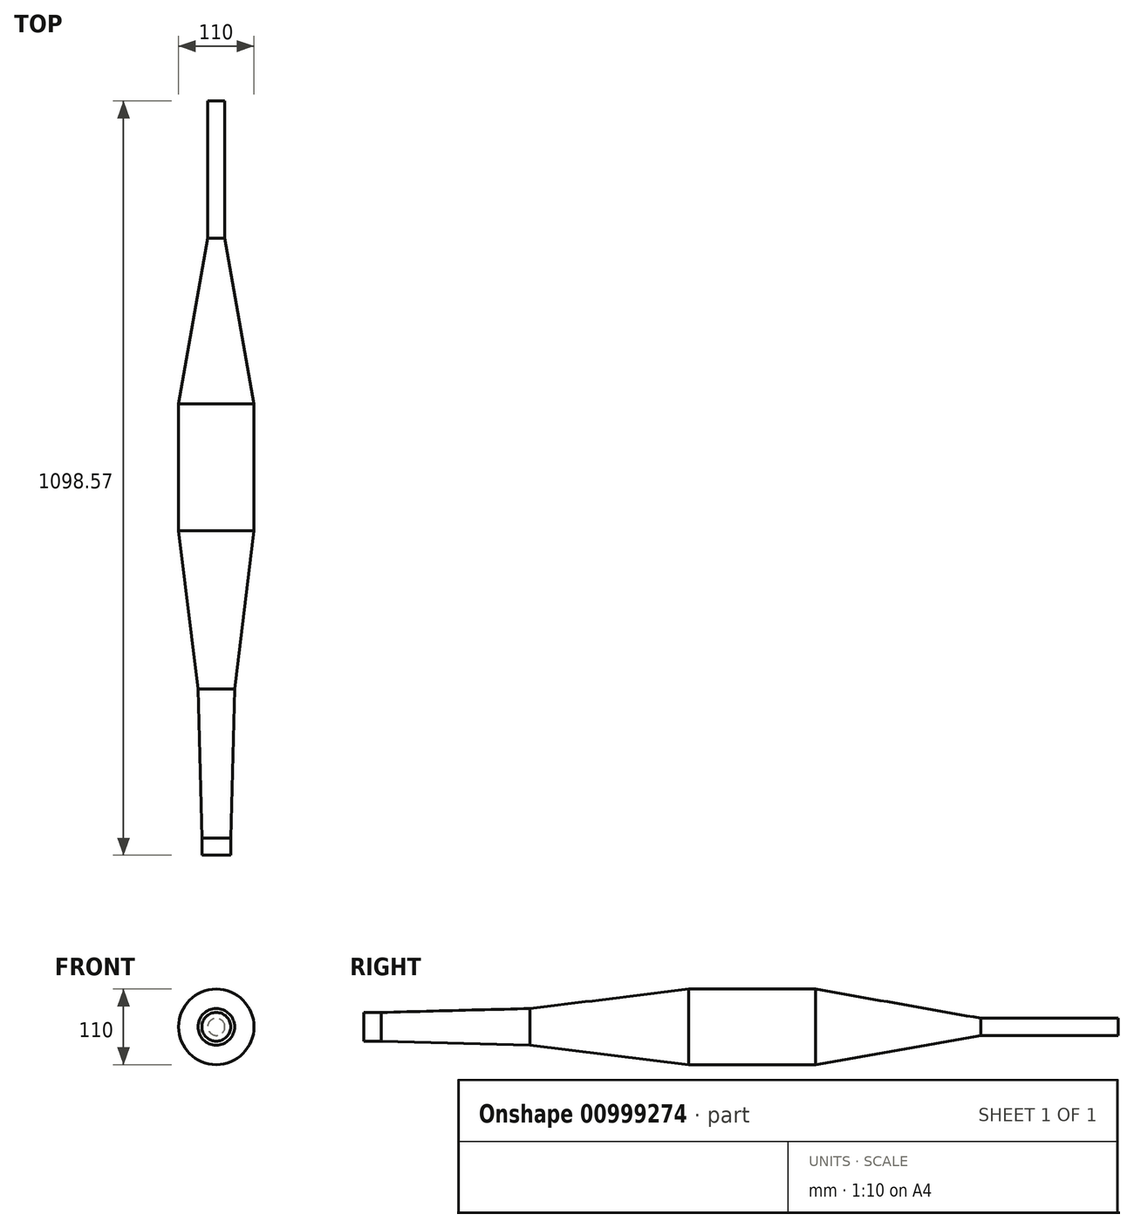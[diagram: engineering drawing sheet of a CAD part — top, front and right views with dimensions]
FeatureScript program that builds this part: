
annotation { "Feature Type Name" : "Feature", "Feature Type Description" : "" }
export const myFeature = defineFeature(function(context is Context, id is Id, definition is map)
    precondition{}
    {
        {
            var Q0;
            Q0=qCreatedBy(makeId("Right.planeOp"),FACE);
            var sketch = newSketch(context, id + "F0", { "sketchPlane" : qUnion([Q0])});
            skLineSegment(sketch, "E0", {"start": v(21.65, -12.5) * mm, "end": v(42.65, 23.87) * mm});
            skLineSegment(sketch, "E1", {"start": v(0, 191.98) * mm, "end": v(0, 233.98) * mm});
            skLineSegment(sketch, "E2", {"start": v(0, 212.98) * mm, "end": v(242, 212.98) * mm});
            skLineSegment(sketch, "E3", {"start": v(0, 212.98) * mm, "end": v(-65, 212.98) * mm});
            skLineSegment(sketch, "E4", {"start": v(242, 239.66) * mm, "end": v(242, 186.3) * mm});
            skLineSegment(sketch, "E5", {"start": v(25, 233.98) * mm, "end": v(242, 239.66) * mm});
            skLineSegment(sketch, "E6", {"start": v(25, 191.98) * mm, "end": v(242, 186.3) * mm});
            skLineSegment(sketch, "E7", {"start": v(-51.1, 50.44) * mm, "end": v(-51.1, 27.44) * mm});
            skLineSegment(sketch, "E8", {"start": v(-51.1, 38.94) * mm, "end": v(10.5, 18.19) * mm});
            skLineSegment(sketch, "E9", {"start": v(242, 212.98) * mm, "end": v(344.06, 212.98) * mm});
            skLineSegment(sketch, "E10", {"start": v(242, 239.66) * mm, "end": v(344.06, 252.2) * mm});
            skLineSegment(sketch, "E11", {"start": v(242, 186.3) * mm, "end": v(344.06, 173.76) * mm});
            skLineSegment(sketch, "E12", {"start": v(344.06, 252.2) * mm, "end": v(344.06, 173.76) * mm});
            skLineSegment(sketch, "E13", {"start": v(344.06, 212.98) * mm, "end": v(472.63, 212.98) * mm});
            skLineSegment(sketch, "E14", {"start": v(472.63, 157.98) * mm, "end": v(472.63, 267.98) * mm});
            skLineSegment(sketch, "E15", {"start": v(344.06, 252.2) * mm, "end": v(472.63, 267.98) * mm});
            skLineSegment(sketch, "E16", {"start": v(344.06, 173.76) * mm, "end": v(472.63, 157.98) * mm});
            skLineSegment(sketch, "E17", {"start": v(472.63, 212.98) * mm, "end": v(813.5, 212.98) * mm});
            skLineSegment(sketch, "E18", {"start": v(813.5, 212.98) * mm, "end": v(898.57, 212.98) * mm});
            skLineSegment(sketch, "E19", {"start": v(898.57, 200.48) * mm, "end": v(898.57, 225.48) * mm});
            skLineSegment(sketch, "E20", {"start": v(657.54, 267.98) * mm, "end": v(969.46, 212.98) * mm, "construction": true});
            skLineSegment(sketch, "E21", {"start": v(969.46, 212.98) * mm, "end": v(657.54, 157.98) * mm, "construction": true});
            skLineSegment(sketch, "E22", {"start": v(472.63, 267.98) * mm, "end": v(657.54, 267.98) * mm});
            skLineSegment(sketch, "E23", {"start": v(472.63, 157.98) * mm, "end": v(657.54, 157.98) * mm});
            skLineSegment(sketch, "E24", {"start": v(813.5, 185.48) * mm, "end": v(813.5, 240.48) * mm});
            skLineSegment(sketch, "E25", {"start": v(657.54, 267.98) * mm, "end": v(657.54, 157.98) * mm});
            skLineSegment(sketch, "E26", {"start": v(898.57, 225.48) * mm, "end": v(1098.57, 225.48) * mm});
            skLineSegment(sketch, "E27", {"start": v(898.57, 200.48) * mm, "end": v(1098.57, 200.48) * mm});
            skLineSegment(sketch, "E28", {"start": v(1098.57, 200.48) * mm, "end": v(1098.57, 225.48) * mm});
            skLineSegment(sketch, "E29", {"start": v(657.54, 267.98) * mm, "end": v(898.57, 225.48) * mm});
            skLineSegment(sketch, "E30", {"start": v(657.54, 157.98) * mm, "end": v(898.57, 200.48) * mm});
            skLineSegment(sketch, "E31", {"start": v(21.65, -12.5) * mm, "end": v(21.65, -190.3) * mm, "construction": true});
            skArc(sketch, "E32", {"start": v(32.15, 5.69) * mm, "mid": v(97.18, -130.66) * mm, "end": v(-6.8, -240.23) * mm, "construction": true});
            skLineSegment(sketch, "E33", {"start": v(-34.52, -109.8) * mm, "end": v(77.31, -182.43) * mm, "construction": true});
            skLineSegment(sketch, "E34", {"start": v(99.7, -196.96) * mm, "end": v(54.93, -167.9) * mm});
            skArc(sketch, "E35", {"start": v(99.7, -196.96) * mm, "mid": v(119.73, -74) * mm, "end": v(42.65, 23.87) * mm});
            skArc(sketch, "E36", {"start": v(54.93, -167.9) * mm, "mid": v(70.55, -83.29) * mm, "end": v(21.65, -12.5) * mm});
            skLineSegment(sketch, "E37", {"start": v(-6.8, -240.23) * mm, "end": v(-132.56, -266.96) * mm, "construction": true});
            skLineSegment(sketch, "E38", {"start": v(1.35, -278.6) * mm, "end": v(-14.95, -201.88) * mm});
            skLineSegment(sketch, "E39", {"start": v(-14.95, -201.88) * mm, "end": v(-144, -213.17) * mm});
            skLineSegment(sketch, "E40", {"start": v(1.35, -278.6) * mm, "end": v(-121.12, -320.76) * mm});
            skLineSegment(sketch, "E41", {"start": v(-144, -213.17) * mm, "end": v(-121.12, -320.76) * mm});
            skLineSegment(sketch, "E42", {"start": v(77.31, -182.43) * mm, "end": v(-6.8, -240.23) * mm, "construction": true});
            skArc(sketch, "E43", {"start": v(-14.95, -201.88) * mm, "mid": v(23.13, -191.34) * mm, "end": v(54.93, -167.9) * mm});
            skArc(sketch, "E44", {"start": v(1.35, -278.6) * mm, "mid": v(57.98, -246.75) * mm, "end": v(99.7, -196.96) * mm});
            skLineSegment(sketch, "E45", {"start": v(-132.56, -266.96) * mm, "end": v(-317.47, -266.96) * mm, "construction": true});
            skLineSegment(sketch, "E46", {"start": v(-328.9, -320.76) * mm, "end": v(-306.03, -213.17) * mm});
            skLineSegment(sketch, "E47", {"start": v(-328.9, -320.76) * mm, "end": v(-132.56, -266.96) * mm, "construction": true});
            skLineSegment(sketch, "E48", {"start": v(-317.47, -266.96) * mm, "end": v(-121.12, -320.76) * mm, "construction": true});
            skLineSegment(sketch, "E49", {"start": v(-306.03, -213.17) * mm, "end": v(-144, -213.17) * mm});
            skLineSegment(sketch, "E50", {"start": v(-121.12, -320.76) * mm, "end": v(-328.9, -320.76) * mm});
            skLineSegment(sketch, "E51", {"start": v(-622.57, -202.11) * mm, "end": v(-306.03, -213.17) * mm, "construction": true});
            skLineSegment(sketch, "E52", {"start": v(-622.57, -202.11) * mm, "end": v(-328.9, -320.76) * mm, "construction": true});
            skLineSegment(sketch, "E53", {"start": v(969.46, 212.98) * mm, "end": v(657.54, 212.98) * mm, "construction": true});
            skLineSegment(sketch, "E54", {"start": v(-317.47, -266.96) * mm, "end": v(-622.57, -202.11) * mm, "construction": true});
            skLineSegment(sketch, "E55", {"start": v(-555.83, -229.08) * mm, "end": v(-550.63, -204.62) * mm});
            skLineSegment(sketch, "E56", {"start": v(-550.63, -204.62) * mm, "end": v(-746.26, -163.04) * mm});
            skLineSegment(sketch, "E57", {"start": v(-746.26, -163.04) * mm, "end": v(-751.46, -187.5) * mm});
            skLineSegment(sketch, "E58", {"start": v(-751.46, -187.5) * mm, "end": v(-555.83, -229.08) * mm});
            skLineSegment(sketch, "E59", {"start": v(-550.63, -204.62) * mm, "end": v(-306.03, -213.17) * mm});
            skLineSegment(sketch, "E60", {"start": v(-555.83, -229.08) * mm, "end": v(-328.9, -320.76) * mm});
            skLineSegment(sketch, "E61", {"start": v(42.65, 23.87) * mm, "end": v(21, 36.37) * mm});
            skLineSegment(sketch, "E62", {"start": v(21, 36.37) * mm, "end": v(0, 0) * mm});
            skLineSegment(sketch, "E63", {"start": v(0, 0) * mm, "end": v(21.65, -12.5) * mm});
            skLineSegment(sketch, "E64", {"start": v(0, 212.98) * mm, "end": v(25, 212.98) * mm});
            skLineSegment(sketch, "E65", {"start": v(25, 233.98) * mm, "end": v(25, 191.98) * mm});
            skLineSegment(sketch, "E66", {"start": v(0, 233.98) * mm, "end": v(25, 233.98) * mm});
            skLineSegment(sketch, "E67", {"start": v(0, 191.98) * mm, "end": v(25, 191.98) * mm});
            skLineSegment(sketch, "E68", {"start": v(-51.1, 27.44) * mm, "end": v(0, 0) * mm});
            skLineSegment(sketch, "E69", {"start": v(-51.1, 50.44) * mm, "end": v(21, 36.37) * mm});
            skLineSegment(sketch, "E70", {"start": v(10.5, 18.19) * mm, "end": v(32.15, 5.69) * mm});
            skLineSegment(sketch, "E71", {"start": v(898.57, 212.98) * mm, "end": v(1098.57, 212.98) * mm});
            skLineSegment(sketch, "E72", {"start": v(657.54, 212.98) * mm, "end": v(657.54, 60.58) * mm, "construction": true});
            skLineSegment(sketch, "E73", {"start": v(657.54, 60.58) * mm, "end": v(929.7, 60.58) * mm});
            skLineSegment(sketch, "E74", {"start": v(657.54, 212.98) * mm, "end": v(929.7, 60.58) * mm, "construction": true});
            skSolve(sketch);
        }
        {
            var Q0;
            {var subQ2=sQuery(id+"F0.wireOp",EDGE,"E64");Q0=makeQuery(id+"F0.imprint","IMPRINT",FACE,{"disambiguationData":[TD([[makeQuery(id+"F0.imprint","IMPRINT",EDGE,{"derivedFrom":subQ2}),1.0]])]});}
            var Q1;
            {var subQ0=sQuery(id+"F0.wireOp",EDGE,"E2");Q1=makeQuery(id+"F0.imprint","IMPRINT",FACE,{"disambiguationData":[TD([[makeQuery(id+"F0.imprint","IMPRINT",EDGE,{"derivedFrom":subQ0}),1.0]])]});}
            var Q2;
            {var subQ0=sQuery(id+"F0.wireOp",EDGE,"E9");Q2=makeQuery(id+"F0.imprint","IMPRINT",FACE,{"disambiguationData":[TD([[makeQuery(id+"F0.imprint","IMPRINT",EDGE,{"derivedFrom":subQ0}),1.0]])]});}
            var Q3;
            {var subQ0=sQuery(id+"F0.wireOp",EDGE,"E13");Q3=makeQuery(id+"F0.imprint","IMPRINT",FACE,{"disambiguationData":[TD([[makeQuery(id+"F0.imprint","IMPRINT",EDGE,{"derivedFrom":subQ0}),1.0]])]});}
            var Q4;
            {var subQ3=sQuery(id+"F0.wireOp",EDGE,"E22");Q4=makeQuery(id+"F0.imprint","IMPRINT",FACE,{"disambiguationData":[TD([[makeQuery(id+"F0.imprint","IMPRINT",EDGE,{"derivedFrom":subQ3}),-1.0]])]});}
            var Q5;
            {var subQ1=sQuery(id+"F0.wireOp",EDGE,"E17");var subQ3=sQuery(id+"F0.wireOp",EDGE,"E25");var subQ4=makeQuery(id+"F0.imprint","INTERSECT",VERTEX,{"derivedFrom":[subQ1,subQ3]});Q5=makeQuery(id+"F0.imprint","IMPRINT",FACE,{"disambiguationData":[TD([[makeQuery(id+"F0.imprint","IMPRINT",EDGE,{"disambiguationData":[TD([[subQ4,-1.0]])],"derivedFrom":subQ1}),1.0]])]});}
            var Q6;
            {var subQ0=sQuery(id+"F0.wireOp",EDGE,"E18");Q6=makeQuery(id+"F0.imprint","IMPRINT",FACE,{"disambiguationData":[TD([[makeQuery(id+"F0.imprint","IMPRINT",EDGE,{"derivedFrom":subQ0}),1.0]])]});}
            var Q7;
            {var subQ2=sQuery(id+"F0.wireOp",EDGE,"E26");Q7=makeQuery(id+"F0.imprint","IMPRINT",FACE,{"disambiguationData":[TD([[makeQuery(id+"F0.imprint","IMPRINT",EDGE,{"derivedFrom":subQ2}),-1.0]])]});}
            var Q8;
            Q8=sQuery(id+"F0.wireOp",EDGE,"E3");
            revolve(context, id + "F1", {"surfaceOperationType" : NewSurfaceOperationType.NEW, "entities" : qUnion([Q0, Q1, Q2, Q3, Q4, Q5, Q6, Q7]), "axis" : qUnion([Q8]), "revolveType" : RevolveType.FULL});
        }
        {
            var Q0;
            {var subQ0=sQuery(id+"F0.wireOp",EDGE,"E61");Q0=makeQuery(id+"F0.imprint","IMPRINT",FACE,{"disambiguationData":[TD([[makeQuery(id+"F0.imprint","IMPRINT",EDGE,{"derivedFrom":subQ0}),1.0]])]});}
            var Q1;
            Q1=sQuery(id+"F0.wireOp",EDGE,"E61");
            var Q2;
            Q2=sQuery(id+"F0.wireOp",EDGE,"E70");
            revolve(context, id + "F2", {"bodyType" : ToolBodyType.SURFACE, "surfaceOperationType" : NewSurfaceOperationType.NEW, "entities" : qUnion([Q0]), "surfaceEntities" : qUnion([Q1]), "axis" : qUnion([Q2]), "revolveType" : RevolveType.FULL});
        }
        {
            var Q0;
            Q0=sQuery(id+"F0.wireOp",EDGE,"E34");
            var Q1;
            {var subQ0=sQuery(id+"F0.wireOp",EDGE,"E36");Q1=makeQuery(id+"F0.imprint","IMPRINT",FACE,{"disambiguationData":[TD([[makeQuery(id+"F0.imprint","IMPRINT",EDGE,{"derivedFrom":subQ0}),-1.0]])]});}
            cPlane(context, id + "F3", {"entities" : qUnion([Q0, Q1]), "cplaneType" : CPlaneType.LINE_ANGLE, "offset" : 0 * mm, "angle" : 90 * degree, "width" : 152.4 * mm, "height" : 152.4 * mm});
        }
        {
            var Q0;
            Q0=qCreatedBy(id+"F3.planeOp",FACE);
            var sketch = newSketch(context, id + "F4", { "sketchPlane" : qUnion([Q0])});
            skCircle(sketch, "E75", {"center": v(0, -164.2) * mm, "radius": 26.68 * mm});
            skSolve(sketch);
        }
        {
            var Q0;
            Q0=makeQuery(id+"F4.imprint","IMPRINT",FACE,{"disambiguationData":[TD([[makeQuery(id+"F4.imprint","IMPRINT",EDGE,{"derivedFrom":sQuery(id+"F4.wireOp",EDGE,"E75")}),1.0]])]});
            var Q1;
            Q1=makeQuery(id+"F2.opRevolve","SWEPT_BODY",BODY,{"disambiguationData":[OSD([sQuery(id+"F0.wireOp",EDGE,"E61")])]});
            var Q2;
            Q2=makeQuery(id+"F2.opRevolve","SWEPT_EDGE",EDGE,{"disambiguationData":[OSD([sQuery(id+"F0.wireOp",VERTEX,"E61.start")])]});
            var Q3;
            Q3=sQuery(id+"F4.wireOp",EDGE,"E75");
            var Q4;
            Q4=sQuery(id+"F0.wireOp",EDGE,"E35");
            var Q5;
            Q5=sQuery(id+"F0.wireOp",EDGE,"E36");
            loft(context, id + "F5", {"bodyType" : ToolBodyType.SURFACE, "operationType" : NewBodyOperationType.ADD, "surfaceOperationType" : NewSurfaceOperationType.ADD, "addGuides" : true, "sheetProfilesArray" : [{ "sheetProfileEntities" : qUnion([Q0]) }, { "sheetProfileEntities" : qUnion([Q1]) }], "wireProfilesArray" : [{ "wireProfileEntities" : qUnion([Q2]) }, { "wireProfileEntities" : qUnion([Q3]) }], "guidesArray" : [{ "guideEntities" : qUnion([Q4]), "guideDerivativeType" : LoftGuideDerivativeType.DEFAULT, "guideDerivativeMagnitude" : 1 }, { "guideEntities" : qUnion([Q5]), "guideDerivativeType" : LoftGuideDerivativeType.DEFAULT, "guideDerivativeMagnitude" : 1 }]});
        }
        {
            var Q0;
            Q0=sQuery(id+"F0.wireOp",EDGE,"E38");
            var Q1;
            {var subQ5=sQuery(id+"F0.wireOp",EDGE,"E43");Q1=makeQuery(id+"F0.imprint","IMPRINT",FACE,{"disambiguationData":[TD([[makeQuery(id+"F0.imprint","IMPRINT",EDGE,{"derivedFrom":subQ5}),-1.0]])]});}
            cPlane(context, id + "F6", {"entities" : qUnion([Q0, Q1]), "cplaneType" : CPlaneType.LINE_ANGLE, "offset" : 25.4 * mm, "angle" : 90 * degree, "width" : 152.4 * mm, "height" : 152.4 * mm});
        }
        {
            var Q0;
            Q0=qCreatedBy(id+"F6.planeOp",FACE);
            var sketch = newSketch(context, id + "F7", { "sketchPlane" : qUnion([Q0])});
            skCircle(sketch, "E76", {"center": v(0, -233.57) * mm, "radius": 39.21 * mm});
            skSolve(sketch);
        }
        {
            var Q1;
            Q1=makeQuery(id+"F5.opLoft","CAP_FACE",FACE,{"disambiguationData":[OSD([makeQuery(id+"F4.imprint","IMPRINT",FACE,{"disambiguationData":[TD([[makeQuery(id+"F4.imprint","IMPRINT",EDGE,{"derivedFrom":sQuery(id+"F4.wireOp",EDGE,"E75")}),1.0]])]})])],"isStart":true});
            var Q2;
            Q2=makeQuery(id+"F7.imprint","IMPRINT",FACE,{"disambiguationData":[TD([[makeQuery(id+"F7.imprint","IMPRINT",EDGE,{"derivedFrom":sQuery(id+"F7.wireOp",EDGE,"E76")}),1.0]])]});
            var Q3;
            Q3=sQuery(id+"F7.wireOp",EDGE,"E76");
            var Q4;
            Q4=makeQuery(id+"F4.imprint","IMPRINT",FACE,{"disambiguationData":[TD([[makeQuery(id+"F4.imprint","IMPRINT",EDGE,{"derivedFrom":sQuery(id+"F4.wireOp",EDGE,"E75")}),1.0]])]});
            var Q5;
            Q5=sQuery(id+"F0.wireOp",EDGE,"E44");
            var Q6;
            Q6=sQuery(id+"F0.wireOp",EDGE,"E43");
            loft(context, id + "F8", {"bodyType" : ToolBodyType.SURFACE, "operationType" : NewBodyOperationType.ADD, "addGuides" : true, "sheetProfilesArray" : [{ "sheetProfileEntities" : qUnion([Q1]) }, { "sheetProfileEntities" : qUnion([Q2]) }], "wireProfilesArray" : [{ "wireProfileEntities" : qUnion([Q3]) }, { "wireProfileEntities" : qUnion([Q4]) }], "guidesArray" : [{ "guideEntities" : qUnion([Q5]), "guideDerivativeType" : LoftGuideDerivativeType.DEFAULT, "guideDerivativeMagnitude" : 1 }, { "guideEntities" : qUnion([Q6]), "guideDerivativeType" : LoftGuideDerivativeType.DEFAULT, "guideDerivativeMagnitude" : 1 }]});
        }
        {
            var Q0;
            Q0=sQuery(id+"F0.wireOp",EDGE,"E41");
            var Q1;
            {var subQ0=sQuery(id+"F0.wireOp",EDGE,"E37");Q1=makeQuery(id+"F0.imprint","IMPRINT",FACE,{"disambiguationData":[TD([[makeQuery(id+"F0.imprint","IMPRINT",EDGE,{"derivedFrom":subQ0}),-1.0]])]});}
            cPlane(context, id + "F9", {"entities" : qUnion([Q0, Q1]), "cplaneType" : CPlaneType.LINE_ANGLE, "offset" : 25.4 * mm, "angle" : 90 * degree, "oppositeDirection" : true, "width" : 152.4 * mm, "height" : 152.4 * mm});
        }
        {
            var Q0;
            Q0=qCreatedBy(id+"F9.planeOp",FACE);
            var sketch = newSketch(context, id + "F10", { "sketchPlane" : qUnion([Q0])});
            skCircle(sketch, "E77", {"center": v(0, -235.32) * mm, "radius": 55 * mm});
            skLineSegment(sketch, "E78", {"start": v(0, -180.32) * mm, "end": v(0, -290.32) * mm, "construction": true});
            skSolve(sketch);
        }
        {
            var Q1;
            Q1=makeQuery(id+"F8.opLoft","CAP_FACE",FACE,{"disambiguationData":[OSD([makeQuery(id+"F7.imprint","IMPRINT",FACE,{"disambiguationData":[TD([[makeQuery(id+"F7.imprint","IMPRINT",EDGE,{"derivedFrom":sQuery(id+"F7.wireOp",EDGE,"E76")}),1.0]])]})])],"isStart":true});
            var Q2;
            Q2=makeQuery(id+"F10.imprint","IMPRINT",FACE,{"disambiguationData":[TD([[makeQuery(id+"F10.imprint","IMPRINT",EDGE,{"derivedFrom":sQuery(id+"F10.wireOp",EDGE,"E77")}),1.0]])]});
            var Q3;
            Q3=sQuery(id+"F7.wireOp",EDGE,"E76");
            var Q4;
            Q4=sQuery(id+"F10.wireOp",EDGE,"E77");
            loft(context, id + "F11", {"bodyType" : ToolBodyType.SURFACE, "surfaceOperationType" : NewSurfaceOperationType.ADD, "sheetProfilesArray" : [{ "sheetProfileEntities" : qUnion([Q1]) }, { "sheetProfileEntities" : qUnion([Q2]) }], "wireProfilesArray" : [{ "wireProfileEntities" : qUnion([Q3]) }, { "wireProfileEntities" : qUnion([Q4]) }]});
        }
        {
            var Q0;
            Q0=sQuery(id+"F0.wireOp",EDGE,"E46");
            var Q1;
            {var subQ0=sQuery(id+"F0.wireOp",EDGE,"E45");Q1=makeQuery(id+"F0.imprint","IMPRINT",FACE,{"disambiguationData":[TD([[makeQuery(id+"F0.imprint","IMPRINT",EDGE,{"derivedFrom":subQ0}),-1.0]])]});}
            cPlane(context, id + "F12", {"entities" : qUnion([Q0, Q1]), "cplaneType" : CPlaneType.LINE_ANGLE, "offset" : 25.4 * mm, "angle" : 83 * degree, "width" : 152.4 * mm, "height" : 152.4 * mm});
        }
        {
            var Q0;
            Q0=qCreatedBy(id+"F12.planeOp",FACE);
            var sketch = newSketch(context, id + "F13", { "sketchPlane" : qUnion([Q0])});
            skCircle(sketch, "E79", {"center": v(-31.08, -327.14) * mm, "radius": 55 * mm, "construction": true});
            skCircle(sketch, "E80", {"center": v(-18.38, -327.14) * mm, "radius": 55 * mm});
            skLineSegment(sketch, "E81", {"start": v(-31.08, -327.14) * mm, "end": v(-18.38, -327.14) * mm, "construction": true});
            skLineSegment(sketch, "E82", {"start": v(-18.38, -272.14) * mm, "end": v(-18.38, -382.14) * mm, "construction": true});
            skSolve(sketch);
        }
        {
            var Q0;
            Q0=sQuery(id+"F13.wireOp",VERTEX,"E82.start");
            var Q1;
            Q1=sQuery(id+"F13.wireOp",VERTEX,"E82.end");
            var Q2;
            Q2=sQuery(id+"F10.wireOp",VERTEX,"E78.start");
            cPlane(context, id + "F14", {"entities" : qUnion([Q0, Q1, Q2]), "cplaneType" : CPlaneType.THREE_POINT, "offset" : 25.4 * mm, "width" : 152.4 * mm, "height" : 152.4 * mm});
        }
        {
            var Q0;
            Q0=qCreatedBy(id+"F14.planeOp",FACE);
            var sketch = newSketch(context, id + "F15", { "sketchPlane" : qUnion([Q0])});
            skLineSegment(sketch, "E83", {"start": v(304.85, -213.25) * mm, "end": v(143.47, -214.84) * mm});
            skSolve(sketch);
        }
        {
            var Q0;
            Q0=makeQuery(id+"F11.opLoft","CAP_FACE",FACE,{"disambiguationData":[OSD([makeQuery(id+"F10.imprint","IMPRINT",FACE,{"disambiguationData":[TD([[makeQuery(id+"F10.imprint","IMPRINT",EDGE,{"derivedFrom":sQuery(id+"F10.wireOp",EDGE,"E77")}),1.0]])]})])],"isStart":true});
            var Q1;
            Q1=makeQuery(id+"F13.imprint","IMPRINT",FACE,{"disambiguationData":[TD([[makeQuery(id+"F13.imprint","IMPRINT",EDGE,{"derivedFrom":sQuery(id+"F13.wireOp",EDGE,"E79")}),1.0]])]});
            var Q2;
            Q2=sQuery(id+"F10.wireOp",EDGE,"E77");
            var Q3;
            Q3=sQuery(id+"F13.wireOp",EDGE,"E80");
            var Q4;
            Q4=sQuery(id+"F15.wireOp",EDGE,"E83");
            loft(context, id + "F16", {"bodyType" : ToolBodyType.SURFACE, "surfaceOperationType" : NewSurfaceOperationType.ADD, "addGuides" : true, "sheetProfilesArray" : [{ "sheetProfileEntities" : qUnion([Q0]) }, { "sheetProfileEntities" : qUnion([Q1]) }], "wireProfilesArray" : [{ "wireProfileEntities" : qUnion([Q2]) }, { "wireProfileEntities" : qUnion([Q3]) }], "guidesArray" : [{ "guideEntities" : qUnion([Q4]), "guideDerivativeType" : LoftGuideDerivativeType.DEFAULT, "guideDerivativeMagnitude" : 1 }]});
        }
        {
            var Q0;
            Q0=sQuery(id+"F0.wireOp",EDGE,"E55");
            cPlane(context, id + "F17", {"entities" : qUnion([Q0]), "cplaneType" : CPlaneType.LINE_ANGLE, "offset" : 25.4 * mm, "angle" : 90 * degree, "width" : 152.4 * mm, "height" : 152.4 * mm});
        }
        {
            var Q0;
            Q0=qCreatedBy(id+"F17.planeOp",FACE);
            var sketch = newSketch(context, id + "F18", { "sketchPlane" : qUnion([Q0])});
            skCircle(sketch, "E84", {"center": v(0, -327.14) * mm, "radius": 12.5 * mm, "construction": true});
            skCircle(sketch, "E85", {"center": v(88.9, -327.14) * mm, "radius": 12.5 * mm});
            skLineSegment(sketch, "E86", {"start": v(0, -327.14) * mm, "end": v(88.9, -327.14) * mm, "construction": true});
            skSolve(sketch);
        }
        {
            var Q0;
            Q0=sQuery(id+"F18.wireOp",EDGE,"E85");
            var Q1;
            Q1=makeQuery(id+"F13.imprint","IMPRINT",FACE,{"disambiguationData":[TD([[makeQuery(id+"F13.imprint","IMPRINT",EDGE,{"derivedFrom":sQuery(id+"F13.wireOp",EDGE,"E80")}),1.0]])]});
            loft(context, id + "F19", {"bodyType" : ToolBodyType.SURFACE, "surfaceOperationType" : NewSurfaceOperationType.ADD, "wireProfilesArray" : [{ "wireProfileEntities" : qUnion([Q0]) }, { "wireProfileEntities" : qUnion([Q1]) }]});
        }
        {
            var Q0;
            Q0=makeQuery(id+"F18.imprint","IMPRINT",FACE,{"disambiguationData":[TD([[makeQuery(id+"F18.imprint","IMPRINT",EDGE,{"derivedFrom":sQuery(id+"F18.wireOp",EDGE,"E85")}),1.0]])]});
            var Q1;
            Q1=sQuery(id+"F18.wireOp",EDGE,"E85");
            extrude(context, id + "F20", {"entities" : qUnion([Q0]), "bodyType" : ToolBodyType.SURFACE, "operationType" : NewBodyOperationType.ADD, "surfaceOperationType" : NewSurfaceOperationType.ADD, "surfaceEntities" : qUnion([Q1]), "oppositeDirection" : true, "depth" : 200 * mm, "offsetDistance" : 25.4 * mm});
        }
    });
